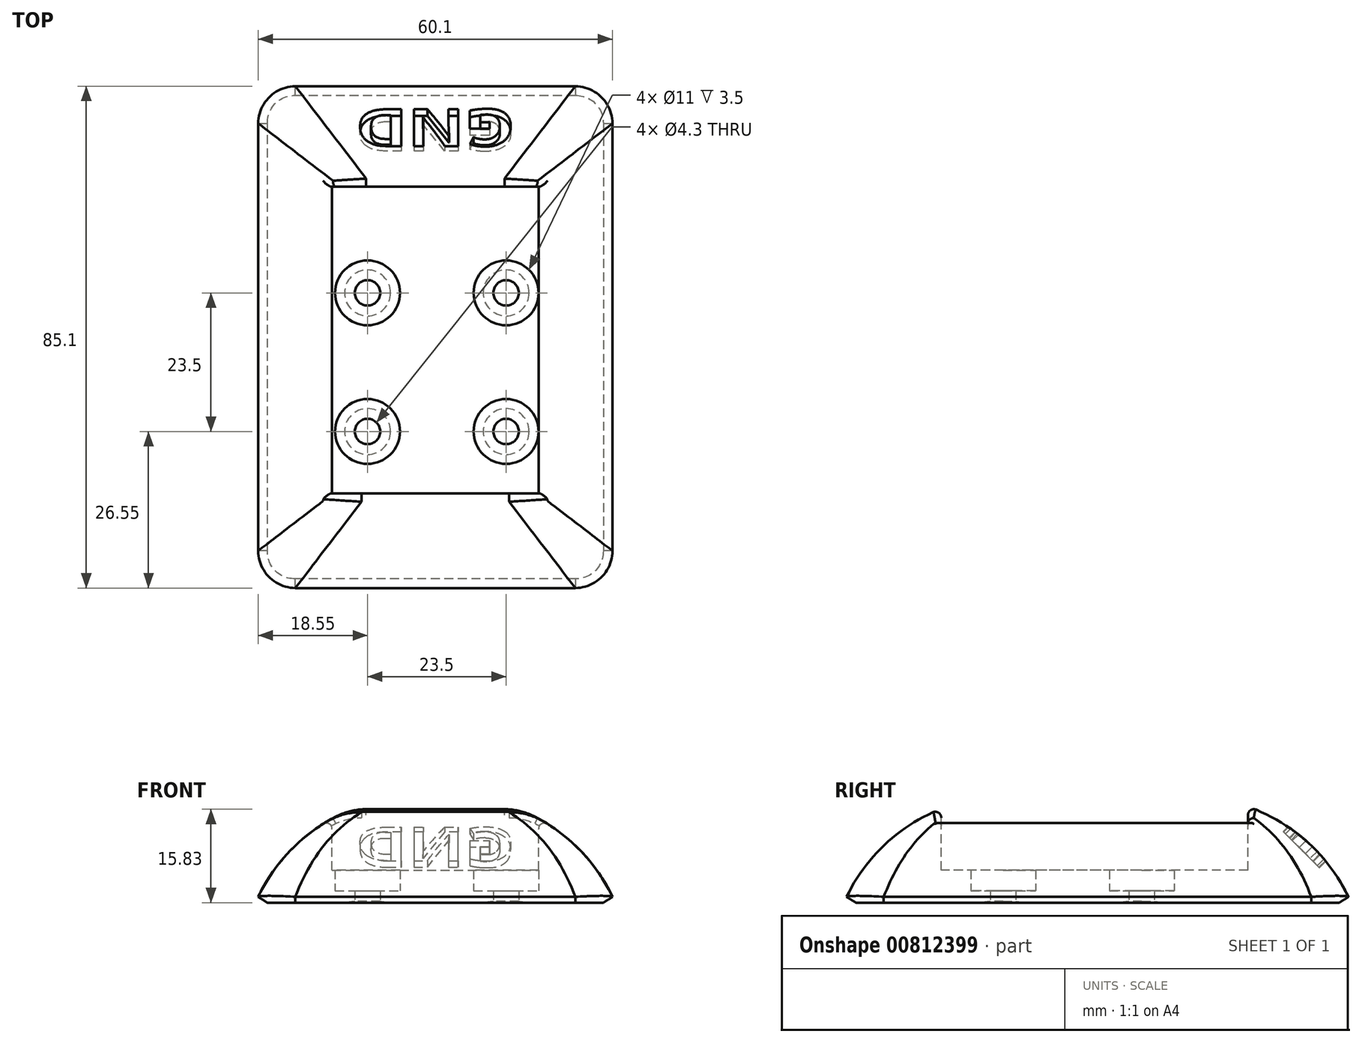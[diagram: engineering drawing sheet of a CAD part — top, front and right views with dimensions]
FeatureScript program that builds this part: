
annotation { "Feature Type Name" : "Feature", "Feature Type Description" : "" }
export const myFeature = defineFeature(function(context is Context, id is Id, definition is map)
    precondition{}
    {
        {
            var Q0;
            Q0=qCreatedBy(makeId("Top.planeOp"),FACE);
            var sketch = newSketch(context, id + "F0", { "sketchPlane" : qUnion([Q0])});
            skLineSegment(sketch, "E0.bottom", {"start": v(-30.5, 43) * mm, "end": v(30.5, 43) * mm});
            skLineSegment(sketch, "E0.top", {"start": v(-30.5, -43) * mm, "end": v(30.5, -43) * mm});
            skLineSegment(sketch, "E0.left", {"start": v(-30.5, 43) * mm, "end": v(-30.5, -43) * mm});
            skLineSegment(sketch, "E0.right", {"start": v(30.5, 43) * mm, "end": v(30.5, -43) * mm});
            skSolve(sketch);
        }
        {
            var Q0;
            Q0=makeQuery(id+"F0.imprint","IMPRINT",FACE,{"disambiguationData":[TD([[makeQuery(id+"F0.imprint","IMPRINT",EDGE,{"derivedFrom":sQuery(id+"F0.wireOp",EDGE,"E0.bottom")}),-1.0]])]});
            extrude(context, id + "F1", {"entities" : qUnion([Q0]), "depth" : 18 * mm, "offsetDistance" : 25 * mm});
        }
        {
            var Q0;
            Q0=makeQuery(id+"F1.opExtrude","CAP_EDGE",EDGE,{"disambiguationData":[OSD([sQuery(id+"F0.wireOp",EDGE,"E0.left")])],"isStart":false});
            var Q1;
            Q1=makeQuery(id+"F1.opExtrude","CAP_EDGE",EDGE,{"disambiguationData":[OSD([sQuery(id+"F0.wireOp",EDGE,"E0.top")])],"isStart":false});
            var Q2;
            Q2=makeQuery(id+"F1.opExtrude","CAP_EDGE",EDGE,{"disambiguationData":[OSD([sQuery(id+"F0.wireOp",EDGE,"E0.right")])],"isStart":false});
            var Q3;
            Q3=makeQuery(id+"F1.opExtrude","CAP_EDGE",EDGE,{"disambiguationData":[OSD([sQuery(id+"F0.wireOp",EDGE,"E0.bottom")])],"isStart":false});
            fillet(context, id + "F2", {"entities" : qUnion([Q0, Q1, Q2, Q3]), "radius" : 30 * mm, "tangentPropagation" : true, "allowEdgeOverflow" : false});
        }
        {
            var Q0;
            Q0=makeQuery(id+"F2.opFillet","BLEND_EDGE",EDGE,{"blendedFrom":[makeQuery(id+"F1.opExtrude","CAP_EDGE",EDGE,{"disambiguationData":[OSD([sQuery(id+"F0.wireOp",EDGE,"E0.bottom")])],"isStart":false}),makeQuery(id+"F1.opExtrude","CAP_EDGE",EDGE,{"disambiguationData":[OSD([sQuery(id+"F0.wireOp",EDGE,"E0.left")])],"isStart":false})],"blendedInto":[]});
            var Q1;
            Q1=makeQuery(id+"F2.opFillet","BLEND_EDGE",EDGE,{"blendedFrom":[makeQuery(id+"F1.opExtrude","CAP_EDGE",EDGE,{"disambiguationData":[OSD([sQuery(id+"F0.wireOp",EDGE,"E0.top")])],"isStart":false}),makeQuery(id+"F1.opExtrude","CAP_EDGE",EDGE,{"disambiguationData":[OSD([sQuery(id+"F0.wireOp",EDGE,"E0.left")])],"isStart":false})],"blendedInto":[]});
            var Q2;
            Q2=makeQuery(id+"F2.opFillet","BLEND_EDGE",EDGE,{"blendedFrom":[makeQuery(id+"F1.opExtrude","CAP_EDGE",EDGE,{"disambiguationData":[OSD([sQuery(id+"F0.wireOp",EDGE,"E0.top")])],"isStart":false}),makeQuery(id+"F1.opExtrude","CAP_EDGE",EDGE,{"disambiguationData":[OSD([sQuery(id+"F0.wireOp",EDGE,"E0.right")])],"isStart":false})],"blendedInto":[]});
            var Q3;
            Q3=makeQuery(id+"F2.opFillet","BLEND_EDGE",EDGE,{"blendedFrom":[makeQuery(id+"F1.opExtrude","CAP_EDGE",EDGE,{"disambiguationData":[OSD([sQuery(id+"F0.wireOp",EDGE,"E0.bottom")])],"isStart":false}),makeQuery(id+"F1.opExtrude","CAP_EDGE",EDGE,{"disambiguationData":[OSD([sQuery(id+"F0.wireOp",EDGE,"E0.right")])],"isStart":false})],"blendedInto":[]});
            fillet(context, id + "F3", {"entities" : qUnion([Q0, Q1, Q2, Q3]), "radius" : 7 * mm, "tangentPropagation" : true, "allowEdgeOverflow" : false});
        }
        {
            var Q0;
            Q0=makeQuery(id+"F1.opExtrude","CAP_FACE",FACE,{"disambiguationData":[OSD([sQuery(id+"F0.wireOp",EDGE,"E0.bottom"),sQuery(id+"F0.wireOp",EDGE,"E0.top"),sQuery(id+"F0.wireOp",EDGE,"E0.left"),sQuery(id+"F0.wireOp",EDGE,"E0.right")])],"isStart":true});
            var sketch = newSketch(context, id + "F4", { "sketchPlane" : qUnion([Q0])});
            skCircle(sketch, "E1", {"center": v(-11.5, 16) * mm, "radius": 2.15 * mm});
            skCircle(sketch, "E2", {"center": v(-11.5, -7.5) * mm, "radius": 2.15 * mm});
            skCircle(sketch, "E3", {"center": v(12, 16) * mm, "radius": 2.15 * mm});
            skCircle(sketch, "E4", {"center": v(12, -7.5) * mm, "radius": 2.15 * mm});
            skCircle(sketch, "E5", {"center": v(-11.5, 16) * mm, "radius": 5.5 * mm});
            skCircle(sketch, "E6", {"center": v(12, 16) * mm, "radius": 5.5 * mm});
            skCircle(sketch, "E7", {"center": v(12, -7.5) * mm, "radius": 5.5 * mm});
            skCircle(sketch, "E8", {"center": v(-11.5, -7.5) * mm, "radius": 5.5 * mm});
            skSolve(sketch);
        }
        {
            var Q0;
            Q0=makeQuery(id+"F4.imprint","IMPRINT",FACE,{"disambiguationData":[TD([[makeQuery(id+"F4.imprint","IMPRINT",EDGE,{"derivedFrom":sQuery(id+"F4.wireOp",EDGE,"E1")}),1.0]])]});
            var Q1;
            Q1=makeQuery(id+"F4.imprint","IMPRINT",FACE,{"disambiguationData":[TD([[makeQuery(id+"F4.imprint","IMPRINT",EDGE,{"derivedFrom":sQuery(id+"F4.wireOp",EDGE,"E3")}),1.0]])]});
            var Q2;
            Q2=makeQuery(id+"F4.imprint","IMPRINT",FACE,{"disambiguationData":[TD([[makeQuery(id+"F4.imprint","IMPRINT",EDGE,{"derivedFrom":sQuery(id+"F4.wireOp",EDGE,"E4")}),1.0]])]});
            var Q3;
            Q3=makeQuery(id+"F4.imprint","IMPRINT",FACE,{"disambiguationData":[TD([[makeQuery(id+"F4.imprint","IMPRINT",EDGE,{"derivedFrom":sQuery(id+"F4.wireOp",EDGE,"E2")}),1.0]])]});
            var Q4;
            Q4=makeQuery(id+"F4.imprint","IMPRINT",FACE,{"disambiguationData":[TD([[makeQuery(id+"F4.imprint","IMPRINT",EDGE,{"derivedFrom":sQuery(id+"F4.wireOp",EDGE,"E1")}),-1.0]])]});
            var Q5;
            Q5=makeQuery(id+"F4.imprint","IMPRINT",FACE,{"disambiguationData":[TD([[makeQuery(id+"F4.imprint","IMPRINT",EDGE,{"derivedFrom":sQuery(id+"F4.wireOp",EDGE,"E3")}),-1.0]])]});
            var Q6;
            Q6=makeQuery(id+"F4.imprint","IMPRINT",FACE,{"disambiguationData":[TD([[makeQuery(id+"F4.imprint","IMPRINT",EDGE,{"derivedFrom":sQuery(id+"F4.wireOp",EDGE,"E4")}),-1.0]])]});
            var Q7;
            Q7=makeQuery(id+"F4.imprint","IMPRINT",FACE,{"disambiguationData":[TD([[makeQuery(id+"F4.imprint","IMPRINT",EDGE,{"derivedFrom":sQuery(id+"F4.wireOp",EDGE,"E2")}),-1.0]])]});
            extrude(context, id + "F5", {"entities" : qUnion([Q0, Q1, Q2, Q3, Q4, Q5, Q6, Q7]), "operationType" : NewBodyOperationType.REMOVE, "oppositeDirection" : true, "depth" : 25 * mm, "offsetDistance" : 25 * mm, "hasSecondDirection" : true, "secondDirectionOppositeDirection" : true, "secondDirectionDepth" : 2 * mm});
        }
        {
            var Q0;
            Q0=makeQuery(id+"F4.imprint","IMPRINT",FACE,{"disambiguationData":[TD([[makeQuery(id+"F4.imprint","IMPRINT",EDGE,{"derivedFrom":sQuery(id+"F4.wireOp",EDGE,"E1")}),1.0]])]});
            var Q1;
            Q1=makeQuery(id+"F4.imprint","IMPRINT",FACE,{"disambiguationData":[TD([[makeQuery(id+"F4.imprint","IMPRINT",EDGE,{"derivedFrom":sQuery(id+"F4.wireOp",EDGE,"E3")}),1.0]])]});
            var Q2;
            Q2=makeQuery(id+"F4.imprint","IMPRINT",FACE,{"disambiguationData":[TD([[makeQuery(id+"F4.imprint","IMPRINT",EDGE,{"derivedFrom":sQuery(id+"F4.wireOp",EDGE,"E2")}),1.0]])]});
            var Q3;
            Q3=makeQuery(id+"F4.imprint","IMPRINT",FACE,{"disambiguationData":[TD([[makeQuery(id+"F4.imprint","IMPRINT",EDGE,{"derivedFrom":sQuery(id+"F4.wireOp",EDGE,"E4")}),1.0]])]});
            extrude(context, id + "F6", {"entities" : qUnion([Q0, Q1, Q2, Q3]), "operationType" : NewBodyOperationType.REMOVE, "oppositeDirection" : true, "depth" : 25 * mm, "offsetDistance" : 25 * mm});
        }
        {
            var Q0;
            {var subQ0=sQuery(id+"F0.wireOp",EDGE,"E0.left");Q0=makeQuery(id+"F2.opFillet","BLEND_EDGE",EDGE,{"blendedFrom":[makeQuery(id+"F1.opExtrude","CAP_EDGE",EDGE,{"disambiguationData":[OSD([subQ0])],"isStart":false}),makeQuery(id+"F1.opExtrude","CAP_FACE",FACE,{"disambiguationData":[OSD([sQuery(id+"F0.wireOp",EDGE,"E0.bottom"),sQuery(id+"F0.wireOp",EDGE,"E0.top"),subQ0,sQuery(id+"F0.wireOp",EDGE,"E0.right")])],"isStart":true})],"blendedInto":[makeQuery(id+"F1.opExtrude","CAP_FACE",FACE,{"disambiguationData":[OSD([sQuery(id+"F0.wireOp",EDGE,"E0.bottom"),sQuery(id+"F0.wireOp",EDGE,"E0.top"),subQ0,sQuery(id+"F0.wireOp",EDGE,"E0.right")])],"isStart":true})]});}
            var Q1;
            Q1=makeQuery(id+"F1.opExtrude","CAP_FACE",FACE,{"disambiguationData":[OSD([sQuery(id+"F0.wireOp",EDGE,"E0.bottom"),sQuery(id+"F0.wireOp",EDGE,"E0.top"),sQuery(id+"F0.wireOp",EDGE,"E0.left"),sQuery(id+"F0.wireOp",EDGE,"E0.right")])],"isStart":true});
            chamfer(context, id + "F7", {"entities" : qUnion([Q0, Q1]), "chamferType" : ChamferType.TWO_OFFSETS, "width1" : 1 * mm, "oppositeDirection" : false, "width2" : 2 * mm, "tangentPropagation" : true});
        }
        {
            var Q0;
            {var subQ0=sQuery(id+"F0.wireOp",EDGE,"E0.bottom");Q0=makeQuery(id+"F7.opChamfer","BLEND_EDGE",EDGE,{"blendedFrom":[makeQuery(id+"F2.opFillet","BLEND_EDGE",EDGE,{"blendedFrom":[makeQuery(id+"F1.opExtrude","CAP_EDGE",EDGE,{"disambiguationData":[OSD([subQ0])],"isStart":false}),makeQuery(id+"F1.opExtrude","CAP_FACE",FACE,{"disambiguationData":[OSD([subQ0,sQuery(id+"F0.wireOp",EDGE,"E0.top"),sQuery(id+"F0.wireOp",EDGE,"E0.left"),sQuery(id+"F0.wireOp",EDGE,"E0.right")])],"isStart":true})],"blendedInto":[makeQuery(id+"F1.opExtrude","CAP_FACE",FACE,{"disambiguationData":[OSD([subQ0,sQuery(id+"F0.wireOp",EDGE,"E0.top"),sQuery(id+"F0.wireOp",EDGE,"E0.left"),sQuery(id+"F0.wireOp",EDGE,"E0.right")])],"isStart":true})]}),makeQuery(id+"F2.opFillet","BLEND_FACE",FACE,{"disambiguationData":[OSD([subQ0])]})],"blendedInto":[makeQuery(id+"F2.opFillet","BLEND_FACE",FACE,{"disambiguationData":[OSD([subQ0])]})]});}
            cPlane(context, id + "F8", {"entities" : qUnion([Q0]), "cplaneType" : CPlaneType.LINE_ANGLE, "offset" : 25 * mm, "angle" : 45 * degree, "width" : 150 * mm, "height" : 150 * mm});
        }
        {
            var Q0;
            Q0=qCreatedBy(id+"F8.planeOp",FACE);
            var sketch = newSketch(context, id + "F9", { "sketchPlane" : qUnion([Q0])});
            skText(sketch, "E9", { "text": "GND", "fontName": "OpenSans-Bold.ttf"});
            const initialGuessF9  = {"E9": [-0.01347, -0.0223, 1, 0, 0.00851]};
            skSetInitialGuess(sketch, initialGuessF9);
            skSolve(sketch);
        }
        {
            var Q0;
            Q0=qSketchRegion(id+"F9",true);
            extrude(context, id + "F10", {"entities" : qUnion([Q0]), "operationType" : NewBodyOperationType.REMOVE, "depth" : 25 * mm, "offsetDistance" : 25 * mm});
        }
        {
            var Q0;
            Q0=makeQuery(id+"F1.opExtrude","CAP_FACE",FACE,{"disambiguationData":[OSD([sQuery(id+"F0.wireOp",EDGE,"E0.bottom"),sQuery(id+"F0.wireOp",EDGE,"E0.top"),sQuery(id+"F0.wireOp",EDGE,"E0.left"),sQuery(id+"F0.wireOp",EDGE,"E0.right")])],"isStart":false});
            var sketch = newSketch(context, id + "F11", { "sketchPlane" : qUnion([Q0])});
            skLineSegment(sketch, "E10.bottom", {"start": v(-17.5, 25.5) * mm, "end": v(17.5, 25.5) * mm});
            skLineSegment(sketch, "E10.top", {"start": v(-17.5, -26.5) * mm, "end": v(17.5, -26.5) * mm});
            skLineSegment(sketch, "E10.left", {"start": v(-17.5, 25.5) * mm, "end": v(-17.5, -26.5) * mm});
            skLineSegment(sketch, "E10.right", {"start": v(17.5, 25.5) * mm, "end": v(17.5, -26.5) * mm});
            skSolve(sketch);
        }
        {
            var Q0;
            Q0=makeQuery(id+"F11.imprint","IMPRINT",FACE,{"disambiguationData":[TD([[makeQuery(id+"F11.imprint","IMPRINT",EDGE,{"derivedFrom":sQuery(id+"F11.wireOp",EDGE,"E10.bottom")}),-1.0]])]});
            var Q1;
            {var subQ0=sQuery(id+"F0.wireOp",EDGE,"E0.right");var subQ1=sQuery(id+"F0.wireOp",EDGE,"E0.left");var subQ2=sQuery(id+"F0.wireOp",EDGE,"E0.top");var subQ3=sQuery(id+"F0.wireOp",EDGE,"E0.bottom");var subQ4=makeQuery(id+"F1.opExtrude","CAP_FACE",FACE,{"disambiguationData":[OSD([subQ3,subQ2,subQ1,subQ0])],"isStart":false});Q1=makeQuery(id+"F11.imprint","IMPRINT",FACE,{"disambiguationData":[TD([[makeQuery(id+"F11.imprint","IMPRINT",EDGE,{"derivedFrom":makeQuery(id+"F2.opFillet","BLEND_EDGE",EDGE,{"blendedFrom":[makeQuery(id+"F1.opExtrude","CAP_EDGE",EDGE,{"disambiguationData":[OSD([subQ3])],"isStart":false}),subQ4],"blendedInto":[subQ4]})}),1.0]])]});}
            extrude(context, id + "F12", {"entities" : qUnion([Q0, Q1]), "operationType" : NewBodyOperationType.REMOVE, "oppositeDirection" : true, "depth" : 12.5 * mm, "offsetDistance" : 25 * mm});
        }
        {
            var Q0;
            {var subQ1=sQuery(id+"F0.wireOp",EDGE,"E0.left");var subQ3=sQuery(id+"F0.wireOp",EDGE,"E0.bottom");Q0=makeQuery(id+"F12.boolean.opBoolean","INTERSECT",EDGE,{"derivedFrom":[makeQuery(id+"F10.boolean.opBoolean","SPLIT",FACE,{"disambiguationData":[TD([makeQuery(id+"F2.opFillet","BLEND_FACE",FACE,{"disambiguationData":[OSD([subQ1])]})])],"derivedFrom":makeQuery(id+"F2.opFillet","BLEND_FACE",FACE,{"disambiguationData":[OSD([subQ3])]})}),makeQuery(id+"F12.opExtrude","SWEPT_FACE",FACE,{"disambiguationData":[OSD([sQuery(id+"F11.wireOp",EDGE,"E10.bottom")])]})]});}
            var Q1;
            Q1=makeQuery(id+"F12.boolean.opBoolean","INTERSECT",EDGE,{"derivedFrom":[makeQuery(id+"F2.opFillet","BLEND_FACE",FACE,{"disambiguationData":[OSD([sQuery(id+"F0.wireOp",EDGE,"E0.left")])]}),makeQuery(id+"F12.opExtrude","SWEPT_FACE",FACE,{"disambiguationData":[OSD([sQuery(id+"F11.wireOp",EDGE,"E10.left")])]})]});
            var Q2;
            Q2=makeQuery(id+"F12.boolean.opBoolean","INTERSECT",EDGE,{"derivedFrom":[makeQuery(id+"F2.opFillet","BLEND_FACE",FACE,{"disambiguationData":[OSD([sQuery(id+"F0.wireOp",EDGE,"E0.right")])]}),makeQuery(id+"F12.opExtrude","SWEPT_FACE",FACE,{"disambiguationData":[OSD([sQuery(id+"F11.wireOp",EDGE,"E10.right")])]})]});
            var Q3;
            Q3=makeQuery(id+"F12.boolean.opBoolean","INTERSECT",EDGE,{"derivedFrom":[makeQuery(id+"F2.opFillet","BLEND_FACE",FACE,{"disambiguationData":[OSD([sQuery(id+"F0.wireOp",EDGE,"E0.top")])]}),makeQuery(id+"F12.opExtrude","SWEPT_FACE",FACE,{"disambiguationData":[OSD([sQuery(id+"F11.wireOp",EDGE,"E10.top")])]})]});
            fillet(context, id + "F13", {"entities" : qUnion([Q0, Q1, Q2, Q3]), "radius" : 1 * mm, "tangentPropagation" : true, "allowEdgeOverflow" : false});
        }
    });
